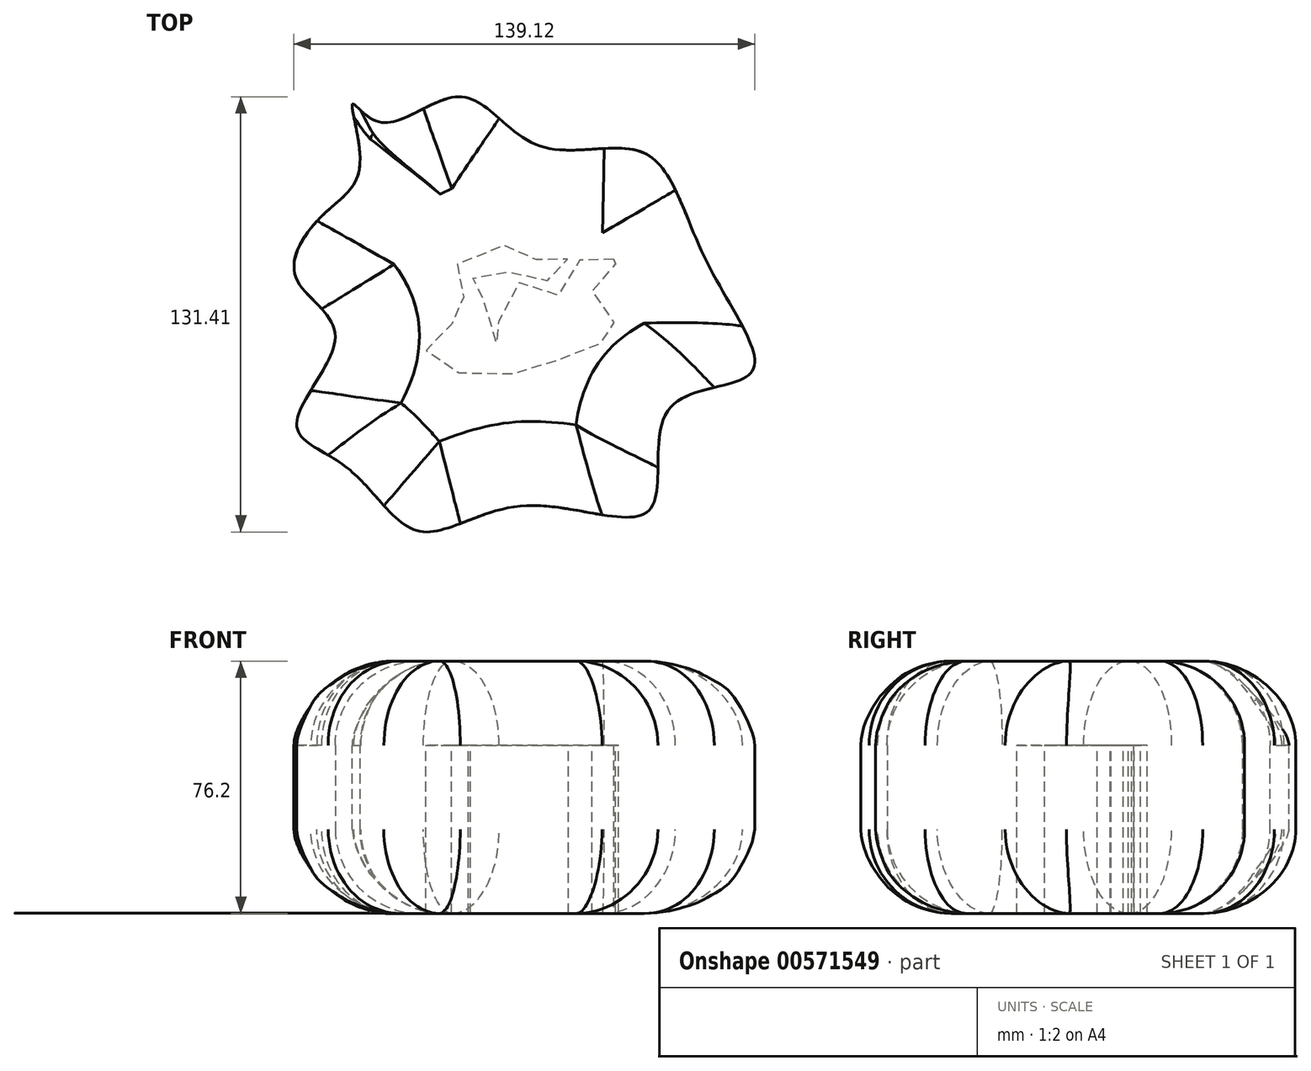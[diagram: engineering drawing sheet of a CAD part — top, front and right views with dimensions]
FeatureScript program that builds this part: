
annotation { "Feature Type Name" : "Feature", "Feature Type Description" : "" }
export const myFeature = defineFeature(function(context is Context, id is Id, definition is map)
    precondition{}
    {
        {
            var Q0;
            Q0=qCreatedBy(makeId("Top.planeOp"),FACE);
            var sketch = newSketch(context, id + "F0", { "sketchPlane" : qUnion([Q0])});
            skFitSpline(sketch, "E0", {"points": [v(-61.12, 28.1) * mm, v(-49.75, 42.85) * mm, v(-51.9, 61.9) * mm, v(-43.61, 56.36) * mm, v(-19.35, 64.04) * mm, v(4.3, 49.3) * mm, v(35.94, 47.15) * mm, v(54.98, 14.28) * mm, v(68.5, -19.2) * mm, v(43.62, -30.25) * mm, v(37.78, -60.66) * mm, v(0, -59.43) * mm, v(-31.94, -67.1) * mm, v(-53.44, -48.07) * mm, v(-68.8, -34.86) * mm, v(-57.13, -7.83) * mm, v(-69.1, 9.68) * mm, v(-61.12, 28.1) * mm]});
            skSolve(sketch);
        }
        {
            var Q0;
            Q0 = qSketchRegion(id + "F0", true);
            extrude(context, id + "F1", {"entities" : qUnion([Q0]), "depth" : 76.2 * mm, "offsetDistance" : 25.4 * mm});
        }
        {
            var Q0;
            Q0=makeQuery(id+"F1.opExtrude","CAP_EDGE",EDGE,{"disambiguationData":[OSD([sQuery(id+"F0.wireOp",EDGE,"E0")])],"isStart":false});
            var Q1;
            Q1=makeQuery(id+"F1.opExtrude","SWEPT_FACE",FACE,{"disambiguationData":[OSD([sQuery(id+"F0.wireOp",EDGE,"E0")])]});
            fillet(context, id + "F2", {"entities" : qUnion([Q0, Q1]), "radius" : 25.4 * mm, "tangentPropagation" : true, "allowEdgeOverflow" : false});
        }
        {
            var Q0;
            Q0=makeQuery(id+"F1.opExtrude","CAP_FACE",FACE,{"disambiguationData":[OSD([sQuery(id+"F0.wireOp",EDGE,"E0")])],"isStart":true});
            var sketch = newSketch(context, id + "F3", { "sketchPlane" : qUnion([Q0])});
            skFitSpline(sketch, "E1", {"points": [v(4.88, -14.48) * mm, v(-5.16, -19.1) * mm, v(-22.03, -10.16) * mm, v(-16.93, 0) * mm, v(-29.27, 9.7) * mm, v(-24.4, 17.66) * mm, v(0, 18.9) * mm, v(18.42, 11.97) * mm, v(28.33, 6.16) * mm, v(20.35, -4.76) * mm, v(27.52, -13.45) * mm, v(18.72, -16.55) * mm, v(9.93, -4.07) * mm, v(-3.93, -7.4) * mm, v(-8.32, 11.74) * mm, v(-10.61, 0) * mm, v(-16.3, -7.78) * mm, v(-8.29, -11.85) * mm, v(6.59, -8.47) * mm, v(13.17, -14.89) * mm, v(4.88, -14.48) * mm]});
            skSolve(sketch);
        }
        {
            var Q0;
            {var subQ0=sQuery(id+"F3.wireOp",EDGE,"E1");var subQ1=sQuery(id+"F0.wireOp",EDGE,"E0");var subQ2=makeQuery(id+"F2.opFillet","BLEND_EDGE",EDGE,{"disambiguationData":[OD(7.0)],"blendedFrom":[makeQuery(id+"F1.opExtrude","CAP_EDGE",EDGE,{"disambiguationData":[OSD([subQ1])],"isStart":true}),makeQuery(id+"F1.opExtrude","CAP_FACE",FACE,{"disambiguationData":[OSD([subQ1])],"isStart":true})],"blendedInto":[makeQuery(id+"F1.opExtrude","CAP_FACE",FACE,{"disambiguationData":[OSD([subQ1])],"isStart":true})]});var subQ3=makeQuery(id+"F3.imprint","INTERSECT",VERTEX,{"disambiguationData":[OD(0.0)],"derivedFrom":[subQ2,subQ0]});Q0=makeQuery(id+"F3.imprint","IMPRINT",FACE,{"disambiguationData":[TD([[makeQuery(id+"F3.imprint","IMPRINT",EDGE,{"disambiguationData":[TD([[subQ3,-1.0]])],"derivedFrom":subQ0}),-1.0]])]});}
            extrude(context, id + "F4", {"entities" : qUnion([Q0]), "operationType" : NewBodyOperationType.REMOVE, "oppositeDirection" : true, "depth" : 50.8 * mm, "offsetDistance" : 25.4 * mm});
        }
    });
